# Revit family: Storage-Credenza-Teknion-B_ZHL_Single_Lateral_File-R2015
name_source: partatom
category: Furniture
revit_build: Autodesk Revit Architecture 2015 (Build: 20140323_1530(x64)
units: mm (PartAtom-declared; Revit-internal decimal feet)

## types (2) — shared parameters
Assembly Code = E2020200
Manufacturer = Teknion
Manufacturer Fax = 416.661.4586
Part Number = BMZHL
Product Documentation Link = http://www.teknion.com
Product Line = Expansion Casegoods
Product Page URL = http://www.teknion.com
Sustainability Data = http://www.teknion.com
URL = http://www.teknion.com
Unit Weight URL = http://www.teknion.com
Warranty = http://www.teknion.com

## per-type parameters (varying)
| type | Description | Model |
| Flush, Full Modesty Panel Style | Credenza with Single Lateral File, 1-3/16" Thick WS, Flush, Full Modesty Panel Style | BMZHL1____ |
| Wall Access Modesty Panel Style | Credenza with Single Lateral File, 1-3/16" Thick WS, Wall Access Modesty Panel Style | BMZHL9____ |

type visibility flags: 2 boolean params named "<type name>" — each type sets only its own to Yes (folded from table)

## geometry (parser evidence)
native form markers: Blend x3, Sweep x2
no freeform markers — native parametric forms only
